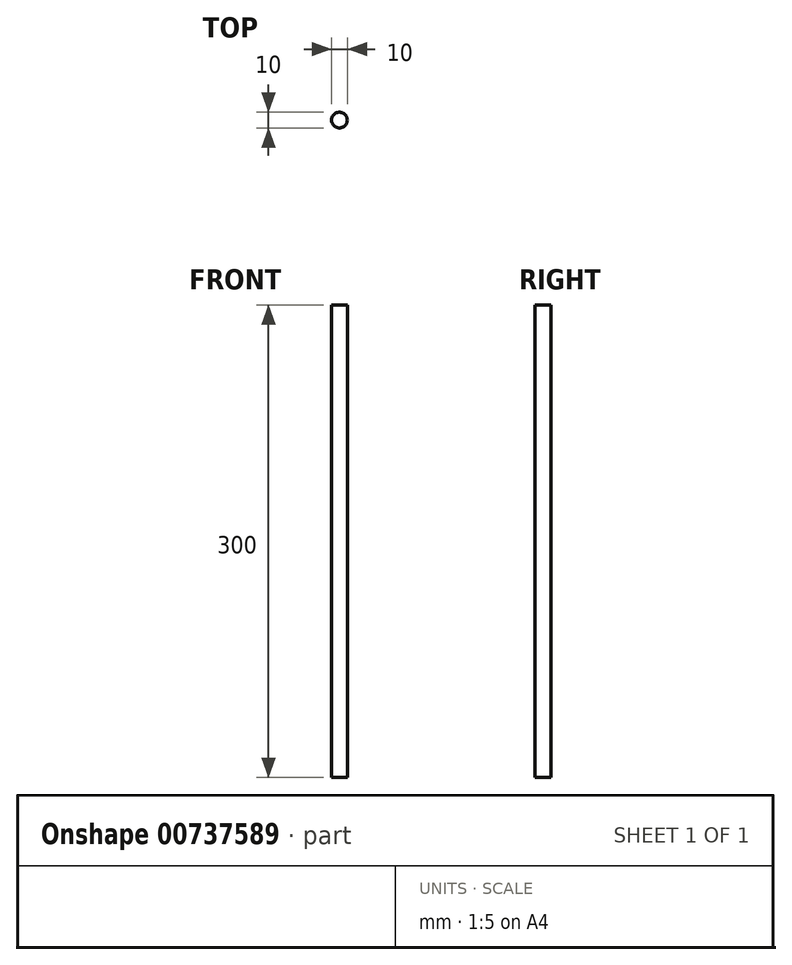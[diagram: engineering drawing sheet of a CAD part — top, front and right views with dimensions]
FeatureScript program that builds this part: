
annotation { "Feature Type Name" : "Feature", "Feature Type Description" : "" }
export const myFeature = defineFeature(function(context is Context, id is Id, definition is map)
    precondition{}
    {
        {
            var Q0;
            Q0=qCreatedBy(makeId("Top.planeOp"),FACE);
            var sketch = newSketch(context, id + "F0", { "sketchPlane" : qUnion([Q0])});
            skCircle(sketch, "E0", {"center": v(0, 0) * mm, "radius": 5 * mm});
            skSolve(sketch);
        }
        {
            var Q0;
            Q0=makeQuery(id+"F0.imprint","IMPRINT",FACE,{"disambiguationData":[TD([[makeQuery(id+"F0.imprint","IMPRINT",EDGE,{"derivedFrom":sQuery(id+"F0.wireOp",EDGE,"E0")}),1.0]])]});
            extrude(context, id + "F1", {"entities" : qUnion([Q0]), "depth" : 300 * mm, "offsetDistance" : 25 * mm});
        }
    });
